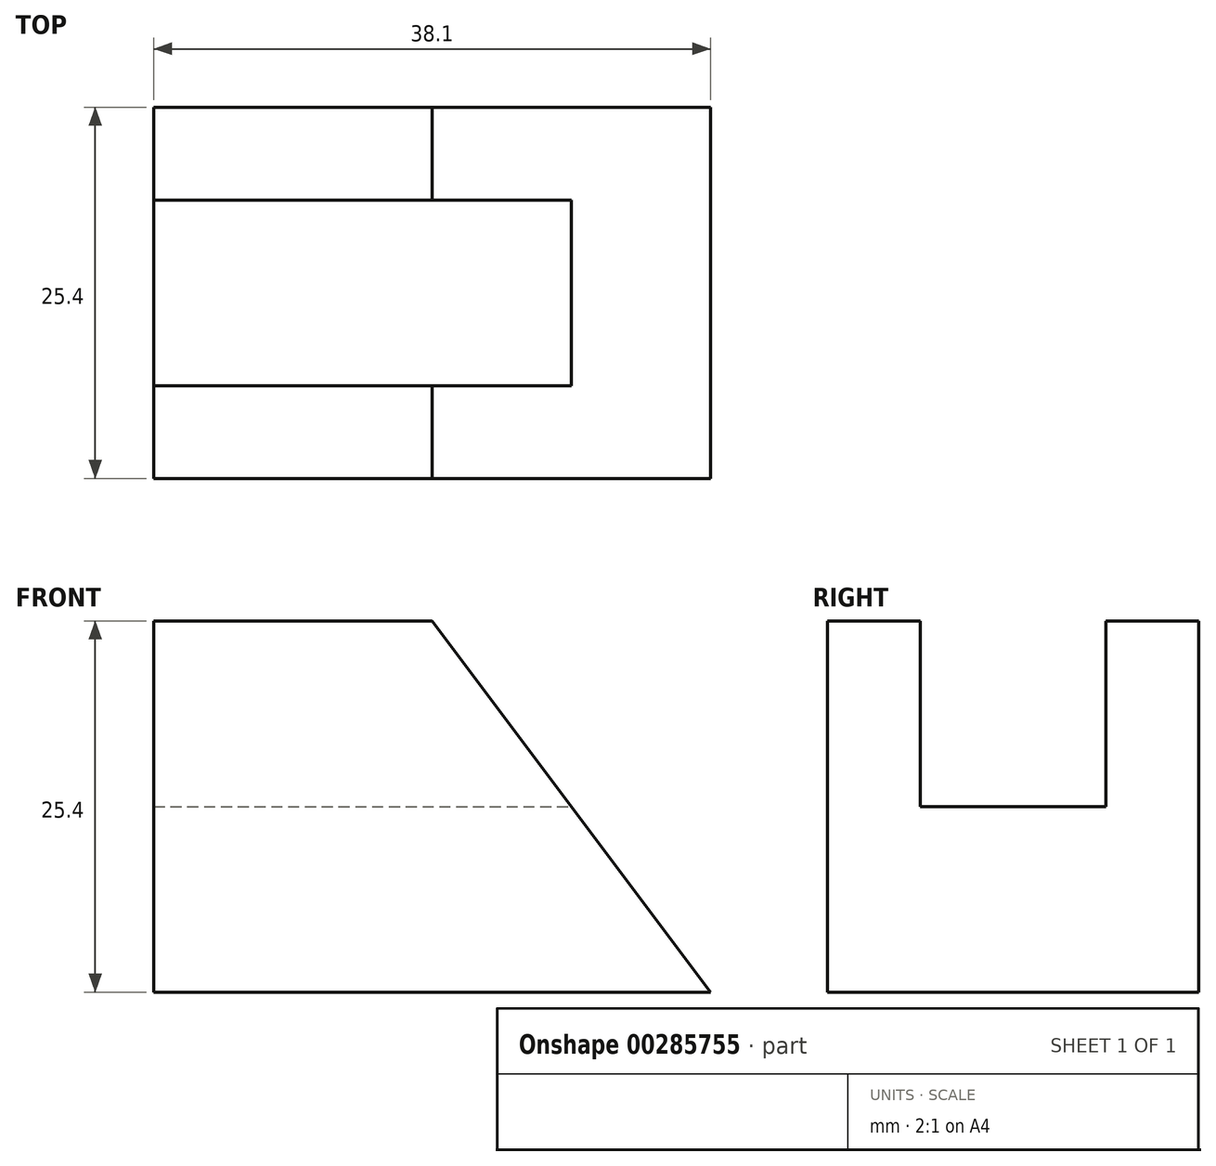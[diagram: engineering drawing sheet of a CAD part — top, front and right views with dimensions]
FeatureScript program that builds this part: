
annotation { "Feature Type Name" : "Feature", "Feature Type Description" : "" }
export const myFeature = defineFeature(function(context is Context, id is Id, definition is map)
    precondition{}
    {
        {
            var Q0;
            Q0=qCreatedBy(makeId("Top.planeOp"),FACE);
            var sketch = newSketch(context, id + "F0", { "sketchPlane" : qUnion([Q0])});
            skLineSegment(sketch, "E0.bottom", {"start": v(0, 0) * mm, "end": v(38.1, 0) * mm});
            skLineSegment(sketch, "E0.top", {"start": v(0, 25.4) * mm, "end": v(38.1, 25.4) * mm});
            skLineSegment(sketch, "E0.left", {"start": v(0, 0) * mm, "end": v(0, 25.4) * mm});
            skLineSegment(sketch, "E0.right", {"start": v(38.1, 0) * mm, "end": v(38.1, 25.4) * mm});
            skSolve(sketch);
        }
        {
            var Q0;
            Q0 = qSketchRegion(id + "F0", true);
            extrude(context, id + "F1", {"entities" : qUnion([Q0]), "oppositeDirection" : true, "depth" : 25.4 * mm});
        }
        {
            var Q0;
            Q0=qCreatedBy(makeId("Top.planeOp"),FACE);
            var sketch = newSketch(context, id + "F2", { "sketchPlane" : qUnion([Q0])});
            skLineSegment(sketch, "E1.bottom", {"start": v(0, 19.05) * mm, "end": v(29.21, 19.05) * mm});
            skLineSegment(sketch, "E1.top", {"start": v(0, 6.35) * mm, "end": v(29.21, 6.35) * mm});
            skLineSegment(sketch, "E1.left", {"start": v(0, 19.05) * mm, "end": v(0, 6.35) * mm});
            skLineSegment(sketch, "E1.right", {"start": v(29.21, 19.05) * mm, "end": v(29.21, 6.35) * mm});
            skLineSegment(sketch, "E2", {"start": v(29.21, 19.05) * mm, "end": v(47.28, 19.05) * mm});
            skLineSegment(sketch, "E3", {"start": v(29.21, 6.35) * mm, "end": v(46.9, 6.35) * mm});
            skLineSegment(sketch, "E4", {"start": v(47.28, 19.05) * mm, "end": v(46.9, 6.35) * mm});
            skSolve(sketch);
        }
        {
            var Q0;
            Q0 = qSketchRegion(id + "F2", true);
            extrude(context, id + "F3", {"entities" : qUnion([Q0]), "operationType" : NewBodyOperationType.REMOVE, "oppositeDirection" : true, "depth" : 12.7 * mm});
        }
        {
            var Q0;
            Q0=qCreatedBy(makeId("Front.planeOp"),FACE);
            var sketch = newSketch(context, id + "F4", { "sketchPlane" : qUnion([Q0])});
            skLineSegment(sketch, "E5", {"start": v(16.27, -25.4) * mm, "end": v(38.1, -25.4) * mm});
            skLineSegment(sketch, "E6", {"start": v(38.1, -25.4) * mm, "end": v(38.1, 0) * mm});
            skLineSegment(sketch, "E7", {"start": v(38.1, 0) * mm, "end": v(38.1, -25.4) * mm});
            skLineSegment(sketch, "E8", {"start": v(38.1, 0) * mm, "end": v(19.05, 0) * mm});
            skLineSegment(sketch, "E9", {"start": v(19.05, 0) * mm, "end": v(38.1, -25.4) * mm});
            skSolve(sketch);
        }
        {
            var Q0;
            Q0 = qSketchRegion(id + "F4", true);
            extrude(context, id + "F5", {"entities" : qUnion([Q0]), "operationType" : NewBodyOperationType.REMOVE, "oppositeDirection" : true, "depth" : 25.4 * mm});
        }
    });
